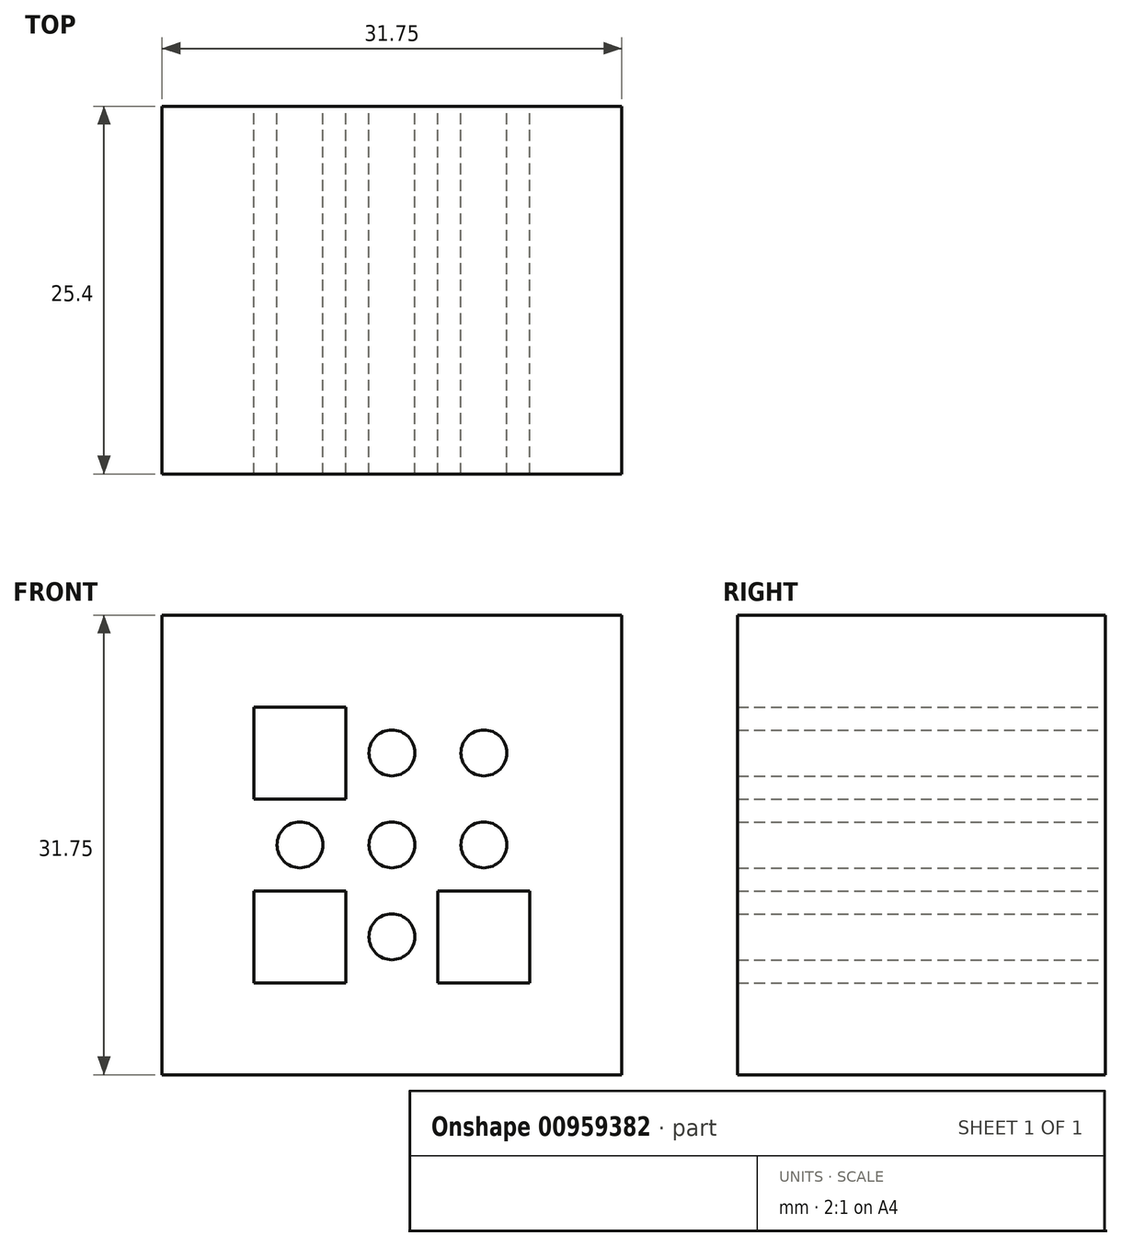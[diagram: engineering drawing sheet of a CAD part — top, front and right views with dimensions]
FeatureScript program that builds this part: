
annotation { "Feature Type Name" : "Feature", "Feature Type Description" : "" }
export const myFeature = defineFeature(function(context is Context, id is Id, definition is map)
    precondition{}
    {
        {
            var Q0;
            Q0=qCreatedBy(makeId("Front.planeOp"),FACE);
            var sketch = newSketch(context, id + "F0", { "sketchPlane" : qUnion([Q0])});
            skLineSegment(sketch, "E0.bottom", {"start": v(10.14, 29.93) * mm, "end": v(-21.6, 29.93) * mm});
            skLineSegment(sketch, "E0.top", {"start": v(10.14, -1.82) * mm, "end": v(-21.6, -1.82) * mm});
            skLineSegment(sketch, "E0.left", {"start": v(10.14, 29.93) * mm, "end": v(10.14, -1.82) * mm});
            skLineSegment(sketch, "E0.right", {"start": v(-21.6, 29.93) * mm, "end": v(-21.6, -1.82) * mm});
            skPoint(sketch, "E0.middle", {"position": v(-5.73, 14.06) * mm});
            skLineSegment(sketch, "E1.bottom", {"start": v(-15.26, 23.58) * mm, "end": v(-8.9, 23.58) * mm});
            skLineSegment(sketch, "E1.top", {"start": v(-15.26, 17.23) * mm, "end": v(-8.9, 17.23) * mm});
            skLineSegment(sketch, "E1.left", {"start": v(-15.26, 23.58) * mm, "end": v(-15.26, 17.23) * mm});
            skLineSegment(sketch, "E1.right", {"start": v(-8.9, 23.58) * mm, "end": v(-8.9, 17.23) * mm});
            skLineSegment(sketch, "E2.bottom", {"start": v(-15.26, 4.53) * mm, "end": v(-8.9, 4.53) * mm});
            skLineSegment(sketch, "E2.top", {"start": v(-15.26, 10.88) * mm, "end": v(-8.9, 10.88) * mm});
            skLineSegment(sketch, "E2.left", {"start": v(-15.26, 4.53) * mm, "end": v(-15.26, 10.88) * mm});
            skLineSegment(sketch, "E2.right", {"start": v(-8.9, 4.53) * mm, "end": v(-8.9, 10.88) * mm});
            skLineSegment(sketch, "E3.bottom", {"start": v(3.8, 4.53) * mm, "end": v(-2.56, 4.53) * mm});
            skLineSegment(sketch, "E3.top", {"start": v(3.8, 10.88) * mm, "end": v(-2.56, 10.88) * mm});
            skLineSegment(sketch, "E3.left", {"start": v(3.8, 4.53) * mm, "end": v(3.8, 10.88) * mm});
            skLineSegment(sketch, "E3.right", {"start": v(-2.56, 4.53) * mm, "end": v(-2.56, 10.88) * mm});
            skCircle(sketch, "E4", {"center": v(-5.73, 7.7) * mm, "radius": 1.59 * mm});
            skCircle(sketch, "E5", {"center": v(-12.08, 14.06) * mm, "radius": 1.59 * mm});
            skCircle(sketch, "E6", {"center": v(-5.73, 14.06) * mm, "radius": 1.59 * mm});
            skCircle(sketch, "E7", {"center": v(-5.73, 20.4) * mm, "radius": 1.59 * mm});
            skCircle(sketch, "E8", {"center": v(0.62, 14.06) * mm, "radius": 1.59 * mm});
            skCircle(sketch, "E9", {"center": v(0.62, 20.4) * mm, "radius": 1.59 * mm});
            skSolve(sketch);
        }
        {
            var Q0;
            Q0=makeQuery(id+"F0.imprint","IMPRINT",FACE,{"disambiguationData":[TD([[makeQuery(id+"F0.imprint","IMPRINT",EDGE,{"derivedFrom":sQuery(id+"F0.wireOp",EDGE,"E0.bottom")}),1.0]])]});
            extrude(context, id + "F1", {"entities" : qUnion([Q0]), "depth" : 25.4 * mm, "offsetDistance" : 25.4 * mm});
        }
        {
            var Q0;
            Q0=makeQuery(id+"F0.imprint","IMPRINT",FACE,{"disambiguationData":[TD([[makeQuery(id+"F0.imprint","IMPRINT",EDGE,{"derivedFrom":sQuery(id+"F0.wireOp",EDGE,"E0.bottom")}),1.0]])]});
            var Q1;
            Q1=makeQuery(id+"F0.imprint","IMPRINT",FACE,{"disambiguationData":[TD([[makeQuery(id+"F0.imprint","IMPRINT",EDGE,{"derivedFrom":sQuery(id+"F0.wireOp",EDGE,"E2.bottom")}),1.0]])]});
            var Q2;
            Q2=makeQuery(id+"F0.imprint","IMPRINT",FACE,{"disambiguationData":[TD([[makeQuery(id+"F0.imprint","IMPRINT",EDGE,{"derivedFrom":sQuery(id+"F0.wireOp",EDGE,"E4")}),1.0]])]});
            var Q3;
            Q3=makeQuery(id+"F0.imprint","IMPRINT",FACE,{"disambiguationData":[TD([[makeQuery(id+"F0.imprint","IMPRINT",EDGE,{"derivedFrom":sQuery(id+"F0.wireOp",EDGE,"E3.bottom")}),-1.0]])]});
            var Q4;
            Q4=makeQuery(id+"F0.imprint","IMPRINT",FACE,{"disambiguationData":[TD([[makeQuery(id+"F0.imprint","IMPRINT",EDGE,{"derivedFrom":sQuery(id+"F0.wireOp",EDGE,"E8")}),1.0]])]});
            var Q5;
            Q5=makeQuery(id+"F0.imprint","IMPRINT",FACE,{"disambiguationData":[TD([[makeQuery(id+"F0.imprint","IMPRINT",EDGE,{"derivedFrom":sQuery(id+"F0.wireOp",EDGE,"E6")}),1.0]])]});
            var Q6;
            Q6=makeQuery(id+"F0.imprint","IMPRINT",FACE,{"disambiguationData":[TD([[makeQuery(id+"F0.imprint","IMPRINT",EDGE,{"derivedFrom":sQuery(id+"F0.wireOp",EDGE,"E5")}),1.0]])]});
            var Q7;
            Q7=makeQuery(id+"F0.imprint","IMPRINT",FACE,{"disambiguationData":[TD([[makeQuery(id+"F0.imprint","IMPRINT",EDGE,{"derivedFrom":sQuery(id+"F0.wireOp",EDGE,"E1.bottom")}),-1.0]])]});
            var Q8;
            Q8=makeQuery(id+"F0.imprint","IMPRINT",FACE,{"disambiguationData":[TD([[makeQuery(id+"F0.imprint","IMPRINT",EDGE,{"derivedFrom":sQuery(id+"F0.wireOp",EDGE,"E7")}),1.0]])]});
            var Q9;
            Q9=makeQuery(id+"F0.imprint","IMPRINT",FACE,{"disambiguationData":[TD([[makeQuery(id+"F0.imprint","IMPRINT",EDGE,{"derivedFrom":sQuery(id+"F0.wireOp",EDGE,"E9")}),1.0]])]});
            extrude(context, id + "F2", {"entities" : qUnion([Q0, Q1, Q2, Q3, Q4, Q5, Q6, Q7, Q8, Q9]), "operationType" : NewBodyOperationType.ADD, "depth" : 1 / 203.2 * mm, "offsetDistance" : 25.4 * mm});
        }
    });
